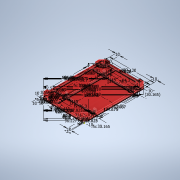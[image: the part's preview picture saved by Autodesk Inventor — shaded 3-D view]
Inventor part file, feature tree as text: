
AUTODESK INVENTOR PART (.ipt)
format: ipt  version: 2021 (Build 250183000, 183)  size: 335,360 bytes
history: native  units: in
note: dims shown in document units (in); Inventor stores cm internally (conversion verified against a paired STEP export)
features: extrude x4, hole x2, other x1
ambient origin geometry x8: Origin, YZ Plane, XZ Plane, XY Plane, X Axis, Y Axis, Z Axis, Center Point
bodies: Body1 (feature_tree)
feature tree (7):
  other  "Base Sketch"
  extrude  "Main Body"  Depth=4.7244in
  extrude  "Structure"  Depth=6.6929in
  extrude  "Corners"  Depth=3.3189in
  extrude  "Board Standoffs"  Depth=4.3177in
  hole  "Standoff Hole"  [1 undecoded]
  hole  "Corner Hole"  [1 undecoded]
note: 2 required parameter values undecoded (feature->parameter linkage not recoverable at this tier; creation-order binding heuristic only, values carry confidence <= 0.55)
